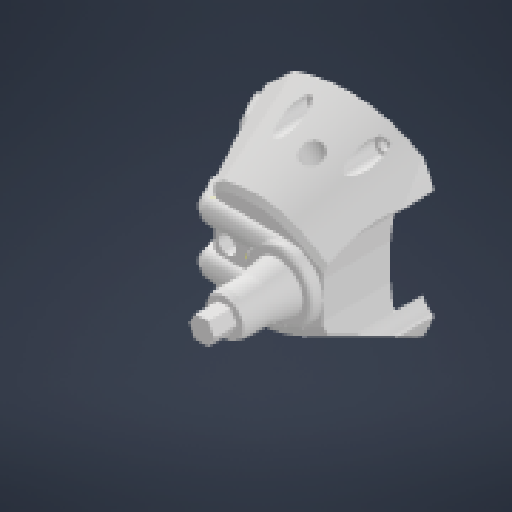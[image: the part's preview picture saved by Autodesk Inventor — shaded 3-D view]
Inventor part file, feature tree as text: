
AUTODESK INVENTOR PART (.ipt)
format: ipt  version: 2024 (Build 280153000, 153)  size: 793,600 bytes
history: native  units: in
note: dims shown in document units (in); Inventor stores cm internally (conversion verified against a paired STEP export)
features: projected_geometry x27, sketch x22, extrude x13, chamfer x13, reference x13, plane x6, sweep x4, other x3, mirror x2, fillet x2
ambient origin geometry x8: Origin, YZ Plane, XZ Plane, XY Plane, X Axis, Y Axis, Z Axis, Center Point
bodies: Solid1 (feature_tree)
feature tree (105):
  extrude  "Extrusion1"  Depth=1.2323in TaperAngle=0.0deg
  extrude  "Extrusion2"  Depth=0.8125in
  chamfer  "Chamfer1"  [1 undecoded]
  plane  "Work Plane1"
  extrude  "Extrusion3"  Depth=0.5in
  plane  "Work Plane2"
  sweep  "Sweep2"
  chamfer  "Chamfer3"  [1 undecoded]
  sweep  "Sweep5"
  sweep  "Sweep6"
  chamfer  "Chamfer4"  Distance=0.3625in
  extrude  "Extrusion4"  TaperAngle=90.0deg  [1 undecoded]
  chamfer  "Chamfer5"  [1 undecoded]
  chamfer  "Chamfer6"  Distance=1.0in
  chamfer  "Chamfer7"  Distance=0.049in
  extrude  "Extrusion5"  Depth=0.5906in
  plane  "Work Plane3"
  sketch  "Sketch18"  dims[d38=0.4033in d39=0.0in d40=0.0in]
  plane  "Work Plane5"
  sweep  "Sweep7"
  plane  "Work Plane6"
  extrude  "Extrusion6"  Depth=0.0787in
  mirror  "Mirror1"
  chamfer  "Chamfer8"  Distance=0.1in
  chamfer  "Chamfer9"  Distance=0.1in
  extrude  "Extrusion7"  Depth=0.2in
  extrude  "Extrusion8"  Depth=0.3937in
  fillet  "Fillet2"  Radius=0.748in
  chamfer  "Chamfer10"  Distance=0.9843in
  chamfer  "Chamfer11"  Distance=0.4375in
  chamfer  "Chamfer12"  Distance=0.0787in
  extrude  "Extrusion11"  Depth=0.3937in
  extrude  "Extrusion12"  Depth=0.3937in TaperAngle=0.0deg
  chamfer  "Chamfer14"  Distance=0.3228in
  fillet  "Fillet3"  Radius=1.0in
  extrude  "Extrusion14"  Depth=0.3937in TaperAngle=75.0deg
  mirror  "Mirror2"
  extrude  "Extrusion15"  Depth=0.3937in TaperAngle=0.0deg
  sketch  "Sketch34"  dims[d108=0.2781in d109=-0.1718in d110=0.3937in d111=0.748in d112=0.9843in d113=0.0in d117=0.4375in d118=0.125in d119=0.0687in d120=0.0787in d121=0.3937in d122=1.7968in d123=0.0in d124=0.3228in d125=1.0in d126=0.0in d127=0.0315in d128=0.125in d129=75.0deg d130=1.0in d131=0.0in]
  chamfer  "Chamfer15"  [1 undecoded]
  plane  "Work Plane7"
  extrude  "Extrusion16"  [1 undecoded]
  sketch  "Sketch1"  dims[d0=0.5394in d1=0.0in d2=1.2323in d3=0.0in]
  reference  "Reference1"
  reference  "Reference2"
  reference  "Reference3"
  sketch  "Sketch2"  dims[d4=0.8in d5=0.125in d6=0.4501in d11=0.8125in]
  reference  "Reference4"
  projected_geometry  "Projected Loop1"
  reference  "Reference5"
  sketch  "Sketch3"  dims[d12=0.0787in]
  reference  "Reference6"
  reference  "Reference7"
  sketch  "Sketch4"  dims[d13=0.0787in]
  projected_geometry  "Projected Loop2"
  sketch  "Sketch5"  dims[d14=0.0787in]
  projected_geometry  "Projected Loop3"
  reference  "Reference8"
  reference  "Reference9"
  reference  "Reference10"
  reference  "Reference11"
  sketch  "Sketch11"  dims[d15=0.0787in]
  projected_geometry  "Projected Loop6"
  sketch  "Sketch12"  dims[d16=0.4823in d17=0.616in d18=0.0in d19=0.0in]
  reference  "Reference14"
  sketch  "Sketch13"  dims[d20=90.0deg d23=0.0in d24=0.0in]
  projected_geometry  "Projected Loop7"
  sketch  "Sketch14"  dims[d30=0.05in d31=0.125in d32=0.4466in d33=0.5in]
  sketch  "Sketch15"  dims[d34=0.5in d35=0.0in d36=0.0in]
  sketch  "Sketch16"  dims[d37=0.4033in]
  reference  "Reference15"
  projected_geometry  "Projected Loop8"
  projected_geometry  "Projected Loop9"
  projected_geometry  "Projected Loop10"
  projected_geometry  "Projected Loop11"
  projected_geometry  "Projected Loop12"
  sketch  "Sketch19"  dims[d41=0.05in d42=0.125in d43=0.4466in d44=0.4823in d45=0.0in]
  sketch  "Sketch20"  dims[d46=0.4875in d47=0.125in d48=0.1718in d49=0.3625in d50=0.125in d51=0.1718in d52=0.3625in d53=0.125in d54=0.1718in]
  projected_geometry  "Projected Loop13"
  sketch  "Sketch22"  dims[d55=1.5448in d56=0.0in d57=90.0deg]
  projected_geometry  "Projected Loop15"
  projected_geometry  "Projected Loop16"
  projected_geometry  "Projected Loop17"
  projected_geometry  "Projected Loop18"
  sketch  "Sketch23"  dims[d59=90.0deg d60=0.0in d61=0.0in]
  projected_geometry  "Projected Loop19"
  sketch  "Sketch24"  dims[d62=90.0deg d63=1.0in d64=0.0in d65=0.049in d66=0.125in d67=0.4398in]
  projected_geometry  "Projected Loop20"
  projected_geometry  "Projected Loop21"
  projected_geometry  "Projected Loop22"
  projected_geometry  "Projected Loop23"
  projected_geometry  "Projected Loop24"
  projected_geometry  "Projected Loop25"
  projected_geometry  "Projected Loop26"
  projected_geometry  "Projected Loop27"
  sketch  "Sketch29"  dims[d68=0.05in d69=0.125in d70=0.4466in d71=0.5906in]
  projected_geometry  "Projected Loop32"
  sketch  "Sketch30"  dims[d72=0.1969in d73=0.0in d74=0.1969in d75=0.0in]
  projected_geometry  "Projected Loop33"
  sketch  "Sketch32"  dims[d80=0.0787in d81=0.1in d82=0.125in d83=0.1718in d84=0.1in d85=0.125in d86=0.1718in d87=0.1in d88=0.125in d89=0.1718in]
  projected_geometry  "Projected Loop35"
  sketch  "Sketch33"  dims[d106=0.2in d107=0.2in]
  other  "<userpath>\Desktop\Camera_Mount.iam"
  other  "Camera_Mount.iam"
  other  "Camera_Baseplate:1"
note: 6 required parameter values undecoded (feature->parameter linkage not recoverable at this tier; creation-order binding heuristic only, values carry confidence <= 0.55)
